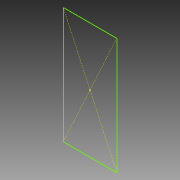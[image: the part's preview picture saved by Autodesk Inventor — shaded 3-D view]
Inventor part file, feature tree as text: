
AUTODESK INVENTOR PART (.ipt)
format: ipt  version: 2015 SP1 (Build 190203100, 203)  size: 59,392 bytes
history: native  units: in
note: dims shown in document units (in); Inventor stores cm internally (conversion verified against a paired STEP export)
features: sketch x1
ambient origin geometry x8: Origin, YZ Plane, XZ Plane, XY Plane, X Axis, Y Axis, Z Axis, Center Point
feature tree (1):
  sketch  "Sketch1"
